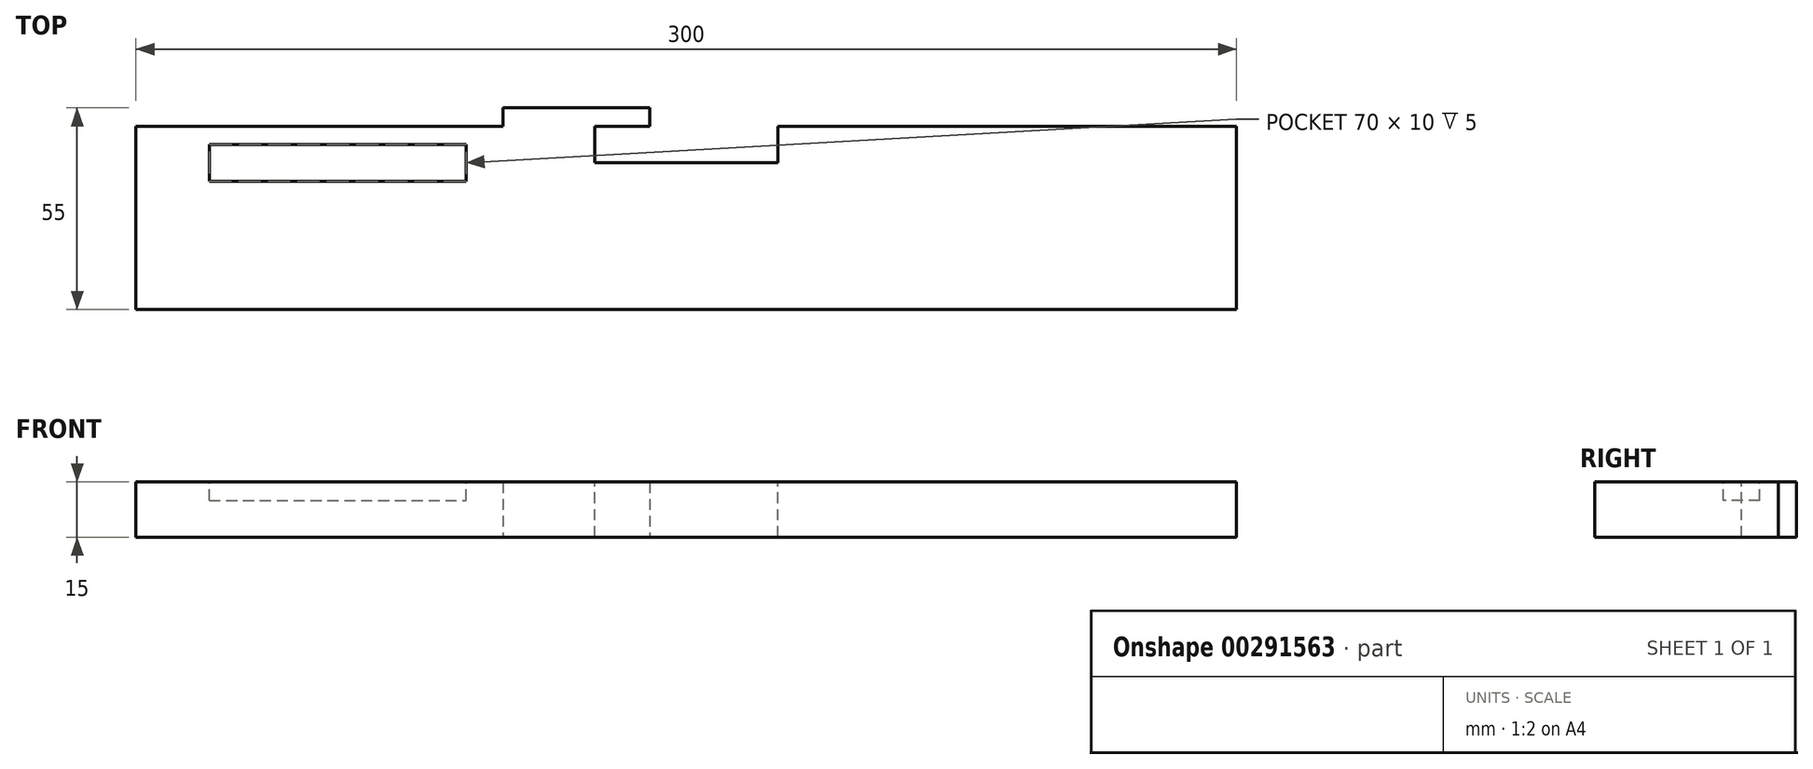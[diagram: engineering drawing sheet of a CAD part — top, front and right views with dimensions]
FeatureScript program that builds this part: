
annotation { "Feature Type Name" : "Feature", "Feature Type Description" : "" }
export const myFeature = defineFeature(function(context is Context, id is Id, definition is map)
    precondition{}
    {
        {
            var Q0;
            Q0=qCreatedBy(makeId("Top.planeOp"),FACE);
            var sketch = newSketch(context, id + "F0", { "sketchPlane" : qUnion([Q0])});
            skLineSegment(sketch, "E0.bottom", {"start": v(-150, 25) * mm, "end": v(150, 25) * mm});
            skLineSegment(sketch, "E0.top", {"start": v(-150, -25) * mm, "end": v(150, -25) * mm});
            skLineSegment(sketch, "E0.left", {"start": v(-150, 25) * mm, "end": v(-150, -25) * mm});
            skLineSegment(sketch, "E0.right", {"start": v(150, 25) * mm, "end": v(150, -25) * mm});
            skLineSegment(sketch, "E1", {"start": v(-171.5, 0) * mm, "end": v(184.76, 0) * mm, "construction": true});
            skLineSegment(sketch, "E2", {"start": v(0, 58.54) * mm, "end": v(0, -58.08) * mm, "construction": true});
            skSolve(sketch);
        }
        {
            var Q0;
            Q0=makeQuery(id+"F0.imprint","IMPRINT",FACE,{"disambiguationData":[TD([[makeQuery(id+"F0.imprint","IMPRINT",EDGE,{"derivedFrom":sQuery(id+"F0.wireOp",EDGE,"E0.bottom")}),-1.0]])]});
            extrude(context, id + "F1", {"entities" : qUnion([Q0]), "depth" : 15 * mm});
        }
        {
            var Q0;
            Q0=makeQuery(id+"F1.opExtrude","CAP_FACE",FACE,{"disambiguationData":[OSD([sQuery(id+"F0.wireOp",EDGE,"E0.bottom"),sQuery(id+"F0.wireOp",EDGE,"E0.top"),sQuery(id+"F0.wireOp",EDGE,"E0.left"),sQuery(id+"F0.wireOp",EDGE,"E0.right")])],"isStart":false});
            var sketch = newSketch(context, id + "F2", { "sketchPlane" : qUnion([Q0])});
            skLineSegment(sketch, "E3.bottom", {"start": v(-25, 25) * mm, "end": v(25, 25) * mm});
            skLineSegment(sketch, "E3.top", {"start": v(-25, 15) * mm, "end": v(25, 15) * mm});
            skLineSegment(sketch, "E3.left", {"start": v(-25, 25) * mm, "end": v(-25, 15) * mm});
            skLineSegment(sketch, "E3.right", {"start": v(25, 25) * mm, "end": v(25, 15) * mm});
            skSolve(sketch);
        }
        {
            var Q0;
            Q0=makeQuery(id+"F2.imprint","IMPRINT",FACE,{"disambiguationData":[TD([[makeQuery(id+"F2.imprint","IMPRINT",EDGE,{"derivedFrom":sQuery(id+"F2.wireOp",EDGE,"E3.bottom")}),-1.0]])]});
            extrude(context, id + "F3", {"entities" : qUnion([Q0]), "operationType" : NewBodyOperationType.REMOVE, "endBound" : BoundingType.THROUGH_ALL, "oppositeDirection" : true, "depth" : 25 * mm});
        }
        {
            var Q0;
            {var subQ1=sQuery(id+"F0.wireOp",EDGE,"E0.left");var subQ3=sQuery(id+"F0.wireOp",EDGE,"E0.bottom");Q0=makeQuery(id+"F3.boolean.opBoolean","SPLIT",FACE,{"disambiguationData":[TD([makeQuery(id+"F1.opExtrude","SWEPT_FACE",FACE,{"disambiguationData":[OSD([subQ1])]})])],"derivedFrom":makeQuery(id+"F1.opExtrude","SWEPT_FACE",FACE,{"disambiguationData":[OSD([subQ3])]})});}
            var sketch = newSketch(context, id + "F4", { "sketchPlane" : qUnion([Q0])});
            skSolve(sketch);
        }
        {
            var Q0;
            {var subQ0=sQuery(id+"F0.wireOp",EDGE,"E0.left");var subQ1=sQuery(id+"F0.wireOp",EDGE,"E0.bottom");Q0=makeQuery(id+"F4.imprint","IMPRINT",FACE,{"disambiguationData":[TD([[makeQuery(id+"F4.imprint","IMPRINT",EDGE,{"derivedFrom":makeQuery(id+"F1.opExtrude","SWEPT_EDGE",EDGE,{"disambiguationData":[OSD([subQ1,subQ0])]})}),-1.0]])]});}
            var sketch = newSketch(context, id + "F5", { "sketchPlane" : qUnion([Q0])});
            skLineSegment(sketch, "E4.bottom", {"start": v(10, 15) * mm, "end": v(50, 15) * mm});
            skLineSegment(sketch, "E4.top", {"start": v(10, 0) * mm, "end": v(50, 0) * mm});
            skLineSegment(sketch, "E4.left", {"start": v(10, 15) * mm, "end": v(10, 0) * mm});
            skLineSegment(sketch, "E4.right", {"start": v(50, 15) * mm, "end": v(50, 0) * mm});
            skSolve(sketch);
        }
        {
            var Q0;
            Q0 = qSketchRegion(id + "F5", true);
            extrude(context, id + "F6", {"entities" : qUnion([Q0]), "operationType" : NewBodyOperationType.ADD, "depth" : 5 * mm});
        }
        {
            var Q0;
            Q0=makeQuery(id+"F6.boolean.opBoolean","MERGE",FACE,{"derivedFrom":[makeQuery(id+"F1.opExtrude","CAP_FACE",FACE,{"disambiguationData":[OSD([sQuery(id+"F0.wireOp",EDGE,"E0.bottom"),sQuery(id+"F0.wireOp",EDGE,"E0.top"),sQuery(id+"F0.wireOp",EDGE,"E0.left"),sQuery(id+"F0.wireOp",EDGE,"E0.right")])],"isStart":false}),makeQuery(id+"F6.opExtrude","SWEPT_FACE",FACE,{"disambiguationData":[OSD([sQuery(id+"F5.wireOp",EDGE,"E4.bottom")])]})]});
            var sketch = newSketch(context, id + "F7", { "sketchPlane" : qUnion([Q0])});
            skLineSegment(sketch, "E5.bottom", {"start": v(-130, 20) * mm, "end": v(-60, 20) * mm});
            skLineSegment(sketch, "E5.top", {"start": v(-130, 10) * mm, "end": v(-60, 10) * mm});
            skLineSegment(sketch, "E5.left", {"start": v(-130, 20) * mm, "end": v(-130, 10) * mm});
            skLineSegment(sketch, "E5.right", {"start": v(-60, 20) * mm, "end": v(-60, 10) * mm});
            skSolve(sketch);
        }
        {
            var Q0;
            Q0 = qSketchRegion(id + "F7", true);
            extrude(context, id + "F8", {"entities" : qUnion([Q0]), "operationType" : NewBodyOperationType.REMOVE, "oppositeDirection" : true, "depth" : 5 * mm});
        }
    });
